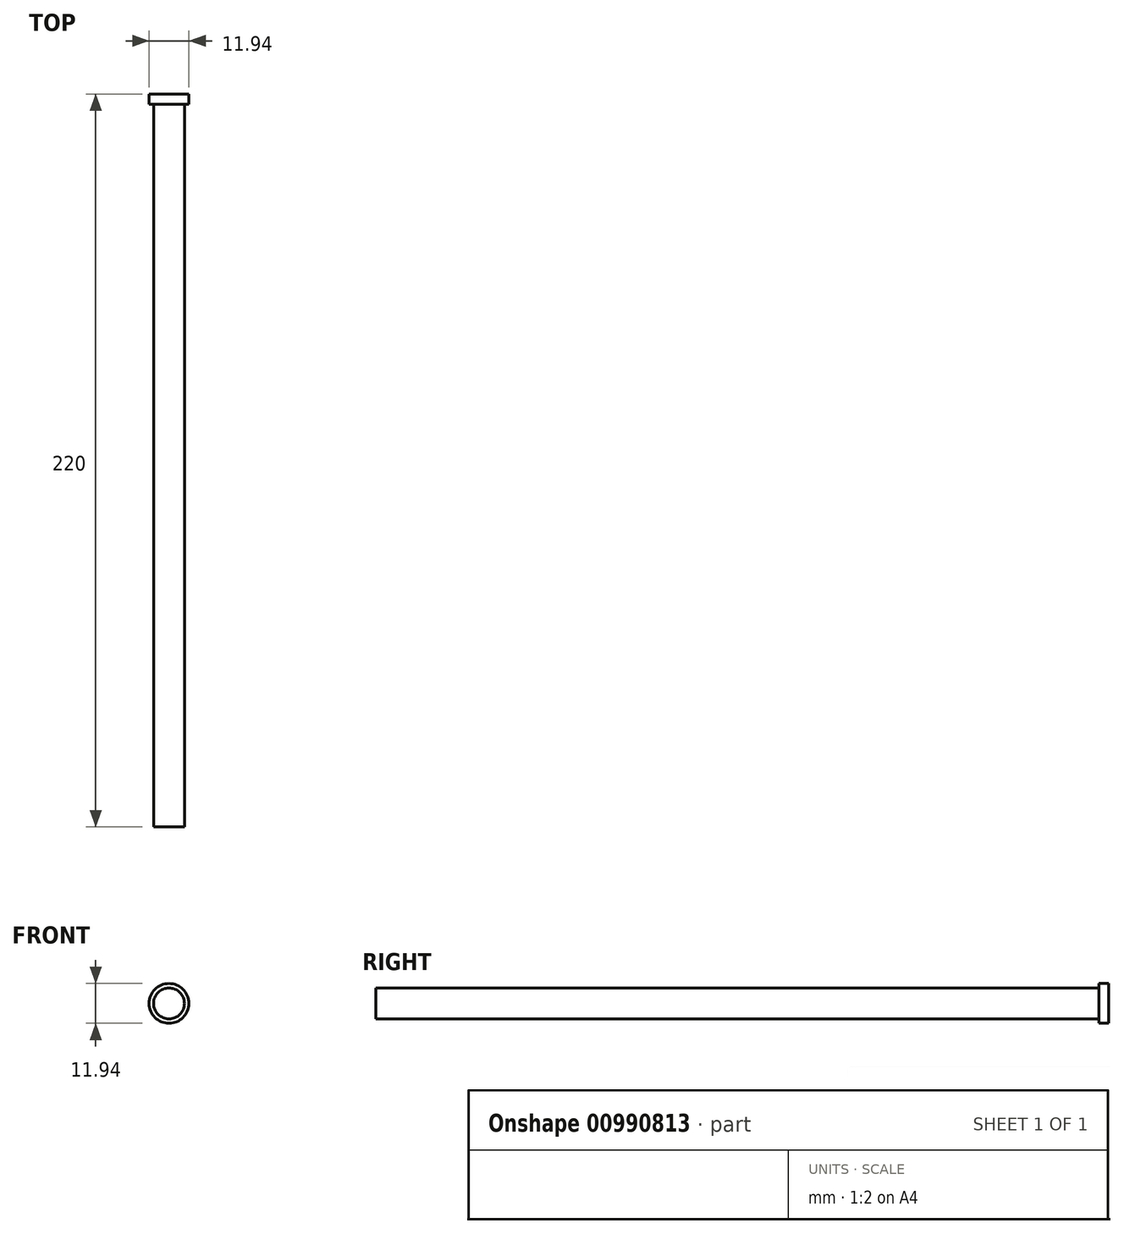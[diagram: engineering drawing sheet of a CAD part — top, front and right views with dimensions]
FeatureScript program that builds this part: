
annotation { "Feature Type Name" : "Feature", "Feature Type Description" : "" }
export const myFeature = defineFeature(function(context is Context, id is Id, definition is map)
    precondition{}
    {
        {
            var Q0;
            Q0=qCreatedBy(makeId("Front.planeOp"),FACE);
            var sketch = newSketch(context, id + "F0", { "sketchPlane" : qUnion([Q0])});
            skCircle(sketch, "E0", {"center": v(0, 0) * mm, "radius": 4.64 * mm});
            skSolve(sketch);
        }
        {
            var Q0;
            Q0 = qSketchRegion(id + "F0", true);
            extrude(context, id + "F1", {"entities" : qUnion([Q0]), "depth" : 220 * mm, "offsetDistance" : 25 * mm});
        }
        {
            var Q0;
            Q0=makeQuery(id+"F1.opExtrude","CAP_FACE",FACE,{"disambiguationData":[OSD([sQuery(id+"F0.wireOp",EDGE,"E0")])],"isStart":true});
            var sketch = newSketch(context, id + "F2", { "sketchPlane" : qUnion([Q0])});
            skCircle(sketch, "E1", {"center": v(0, 0) * mm, "radius": 5.96 * mm});
            skSolve(sketch);
        }
        {
            var Q0;
            Q0 = qSketchRegion(id + "F2", true);
            extrude(context, id + "F3", {"entities" : qUnion([Q0]), "operationType" : NewBodyOperationType.ADD, "oppositeDirection" : true, "depth" : 3 * mm, "offsetDistance" : 25 * mm});
        }
    });
